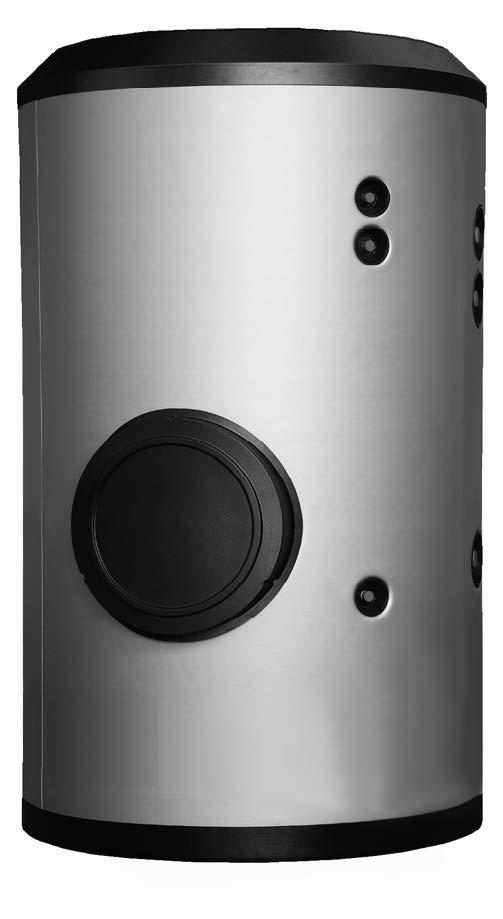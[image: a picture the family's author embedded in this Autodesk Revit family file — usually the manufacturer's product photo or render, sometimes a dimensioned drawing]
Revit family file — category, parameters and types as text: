
# Revit family: IMXV-3000SB_CC01834
name_source: partatom
category: Aparatos eléctricos
revit_build: Autodesk Revit 2016 (Build: 20150220_1215(x64)
units: mm (PartAtom-declared; Revit-internal decimal feet)

## family parameters
Compartido = No
Corte con vacíos al cargar = No
Número OmniClass = 23.80.00.00
Punto de cálculo de habitación = No
Se basa en plano de trabajo = No
Siempre vertical = Sí
Título OmniClass = Electric Power and Lighting

## types (1)
- Depósitos gran capacidad IMXV-SB
    Clase eficiencia energética = C
    Costo = 0 $
    Código de montaje = CC01834
    Descripción = DEPÓSITOS GRAN CAPACIDAD VITRIFICADOS ACERO INOX:
    Dimensiones = 1660 x 2305 mm
    Fabricante = SALVADOR ESCODA
    Imagen de tipo = RB-IMXV.jpg
    Modelo = IMXV 3000 SB
    Peso en vacío = 537 Kg
    Presión máx. circuito = 25 bar
    Presión máx. depósito = 8 bar
    Superfície intercambio = 8,4 m2
    Temperatura máx. ACS = 90 ºC
    Temperatura máx. circuito = 120 ºC
    URL = www.salvadorescoda.com
    Volúmen = 3000 l
